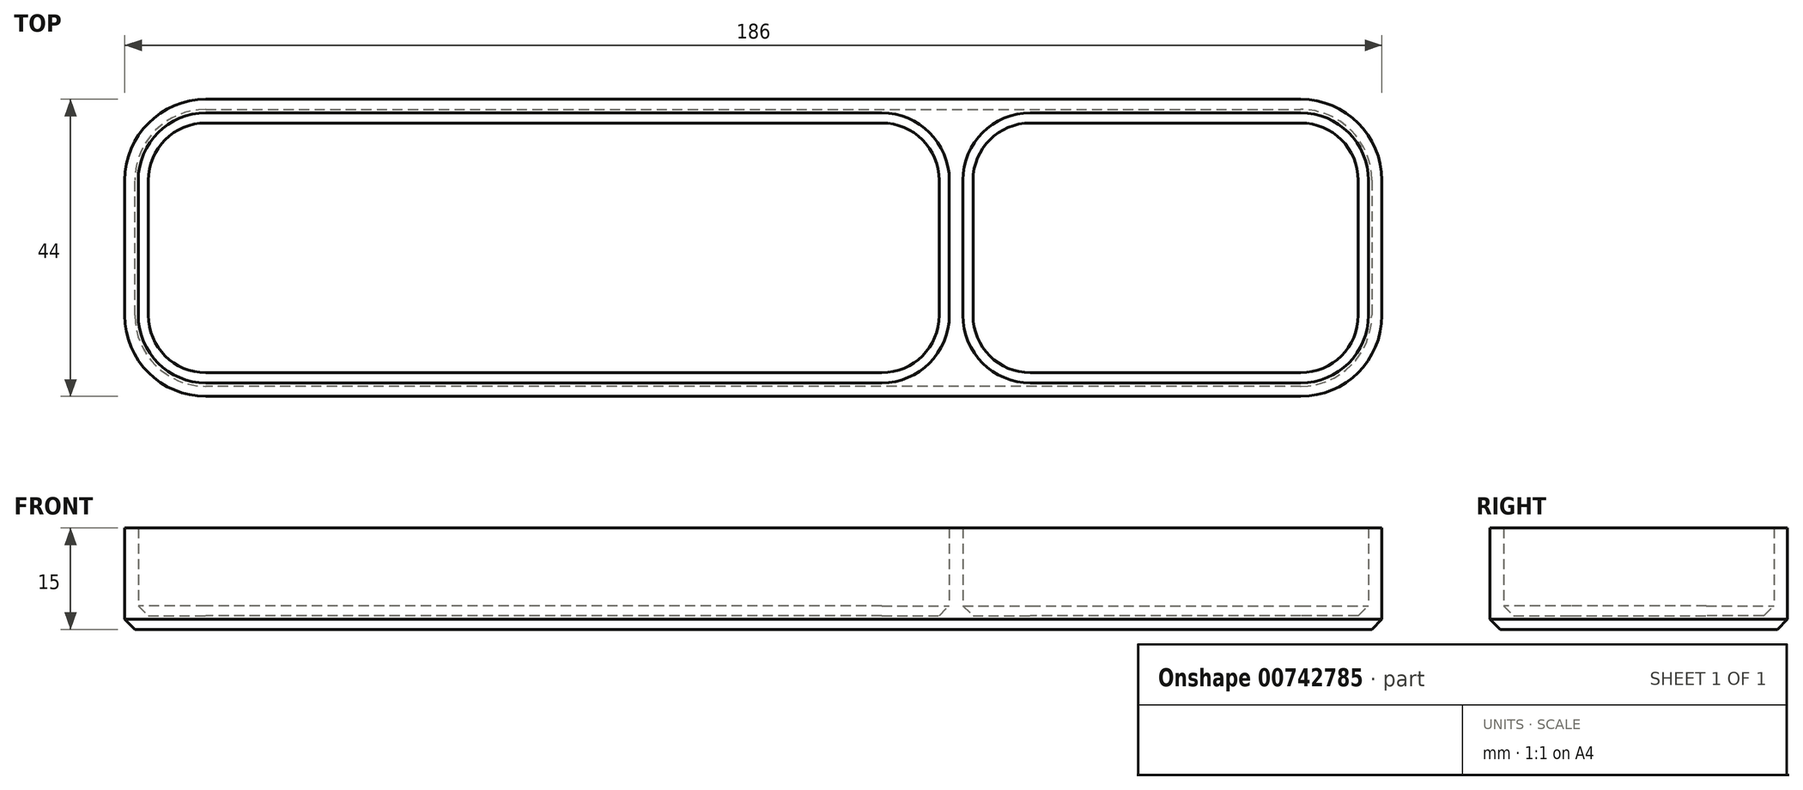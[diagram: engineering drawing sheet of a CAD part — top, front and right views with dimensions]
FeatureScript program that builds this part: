
annotation { "Feature Type Name" : "Feature", "Feature Type Description" : "" }
export const myFeature = defineFeature(function(context is Context, id is Id, definition is map)
    precondition{}
    {
        {
            var Q0;
            Q0=qCreatedBy(makeId("Top.planeOp"),FACE);
            var sketch = newSketch(context, id + "F0", { "sketchPlane" : qUnion([Q0])});
            skLineSegment(sketch, "E0.bottom", {"start": v(10, 0) * mm, "end": v(110, 0) * mm});
            skLineSegment(sketch, "E0.top", {"start": v(10, 40) * mm, "end": v(110, 40) * mm});
            skLineSegment(sketch, "E0.left", {"start": v(0, 10) * mm, "end": v(0, 30) * mm});
            skLineSegment(sketch, "E0.right", {"start": v(120, 10) * mm, "end": v(120, 30) * mm});
            skLineSegment(sketch, "E1.bottom", {"start": v(132, 40) * mm, "end": v(172, 40) * mm});
            skLineSegment(sketch, "E1.top", {"start": v(132, 0) * mm, "end": v(172, 0) * mm});
            skLineSegment(sketch, "E1.left", {"start": v(122, 30) * mm, "end": v(122, 10) * mm});
            skLineSegment(sketch, "E1.right", {"start": v(182, 30) * mm, "end": v(182, 10) * mm});
            skPoint(sketch, "E2.visualSharp", {"position": v(0, 40) * mm});
            skArc(sketch, "E2.filletArc", {"start": v(10, 40) * mm, "mid": v(2.93, 37.07) * mm, "end": v(0, 30) * mm});
            skPoint(sketch, "E3.visualSharp", {"position": v(120, 40) * mm});
            skArc(sketch, "E3.filletArc", {"start": v(120, 30) * mm, "mid": v(117.07, 37.07) * mm, "end": v(110, 40) * mm});
            skPoint(sketch, "E4.visualSharp", {"position": v(120, 0) * mm});
            skArc(sketch, "E4.filletArc", {"start": v(110, 0) * mm, "mid": v(117.07, 2.93) * mm, "end": v(120, 10) * mm});
            skPoint(sketch, "E5.visualSharp", {"position": v(0, 0) * mm});
            skArc(sketch, "E5.filletArc", {"start": v(0, 10) * mm, "mid": v(2.93, 2.93) * mm, "end": v(10, 0) * mm});
            skPoint(sketch, "E6.visualSharp", {"position": v(122, 40) * mm});
            skArc(sketch, "E6.filletArc", {"start": v(132, 40) * mm, "mid": v(124.93, 37.07) * mm, "end": v(122, 30) * mm});
            skPoint(sketch, "E7.visualSharp", {"position": v(122, 0) * mm});
            skArc(sketch, "E7.filletArc", {"start": v(122, 10) * mm, "mid": v(124.93, 2.93) * mm, "end": v(132, 0) * mm});
            skPoint(sketch, "E8.visualSharp", {"position": v(182, 40) * mm});
            skArc(sketch, "E8.filletArc", {"start": v(182, 30) * mm, "mid": v(179.07, 37.07) * mm, "end": v(172, 40) * mm});
            skPoint(sketch, "E9.visualSharp", {"position": v(182, 0) * mm});
            skArc(sketch, "E9.filletArc", {"start": v(172, 0) * mm, "mid": v(179.07, 2.93) * mm, "end": v(182, 10) * mm});
            skLineSegment(sketch, "E10.bottom", {"start": v(-2, 42) * mm, "end": v(184, 42) * mm});
            skLineSegment(sketch, "E10.top", {"start": v(-2, -2) * mm, "end": v(184, -2) * mm});
            skLineSegment(sketch, "E10.left", {"start": v(-2, 42) * mm, "end": v(-2, -2) * mm});
            skLineSegment(sketch, "E10.right", {"start": v(184, 42) * mm, "end": v(184, -2) * mm});
            skSolve(sketch);
        }
        {
            var Q0;
            Q0 = qSketchRegion(id + "F0", true);
            extrude(context, id + "F1", {"entities" : qUnion([Q0]), "depth" : 15 * mm, "offsetDistance" : 25 * mm});
        }
        {
            var Q0;
            Q0=makeQuery(id+"F1.opExtrude","CAP_FACE",FACE,{"disambiguationData":[OSD([sQuery(id+"F0.wireOp",EDGE,"E0.bottom"),sQuery(id+"F0.wireOp",EDGE,"E0.top"),sQuery(id+"F0.wireOp",EDGE,"E0.left"),sQuery(id+"F0.wireOp",EDGE,"E0.right"),sQuery(id+"F0.wireOp",EDGE,"E1.bottom"),sQuery(id+"F0.wireOp",EDGE,"E1.top"),sQuery(id+"F0.wireOp",EDGE,"E1.left"),sQuery(id+"F0.wireOp",EDGE,"E1.right"),sQuery(id+"F0.wireOp",EDGE,"E2.filletArc"),sQuery(id+"F0.wireOp",EDGE,"E3.filletArc"),sQuery(id+"F0.wireOp",EDGE,"E4.filletArc"),sQuery(id+"F0.wireOp",EDGE,"E5.filletArc"),sQuery(id+"F0.wireOp",EDGE,"E6.filletArc"),sQuery(id+"F0.wireOp",EDGE,"E7.filletArc"),sQuery(id+"F0.wireOp",EDGE,"E8.filletArc"),sQuery(id+"F0.wireOp",EDGE,"E9.filletArc"),sQuery(id+"F0.wireOp",EDGE,"E10.bottom"),sQuery(id+"F0.wireOp",EDGE,"E10.top"),sQuery(id+"F0.wireOp",EDGE,"E10.left"),sQuery(id+"F0.wireOp",EDGE,"E10.right")])],"isStart":true});
            var sketch = newSketch(context, id + "F2", { "sketchPlane" : qUnion([Q0])});
            skLineSegment(sketch, "E11.bottom", {"start": v(-2, 2) * mm, "end": v(184, 2) * mm});
            skLineSegment(sketch, "E11.top", {"start": v(-2, -42) * mm, "end": v(184, -42) * mm});
            skLineSegment(sketch, "E11.left", {"start": v(-2, 2) * mm, "end": v(-2, -42) * mm});
            skLineSegment(sketch, "E11.right", {"start": v(184, 2) * mm, "end": v(184, -42) * mm});
            skSolve(sketch);
        }
        {
            var Q0;
            Q0 = qSketchRegion(id + "F2", true);
            extrude(context, id + "F3", {"entities" : qUnion([Q0]), "operationType" : NewBodyOperationType.ADD, "oppositeDirection" : true, "depth" : 2 * mm, "offsetDistance" : 25 * mm});
        }
        {
            var Q0;
            Q0=makeQuery(id+"F1.opExtrude","SWEPT_EDGE",EDGE,{"disambiguationData":[OSD([sQuery(id+"F0.wireOp",EDGE,"E10.top"),sQuery(id+"F0.wireOp",EDGE,"E10.left")])]});
            var Q1;
            Q1=makeQuery(id+"F1.opExtrude","SWEPT_EDGE",EDGE,{"disambiguationData":[OSD([sQuery(id+"F0.wireOp",EDGE,"E10.bottom"),sQuery(id+"F0.wireOp",EDGE,"E10.left")])]});
            var Q2;
            Q2=makeQuery(id+"F1.opExtrude","SWEPT_EDGE",EDGE,{"disambiguationData":[OSD([sQuery(id+"F0.wireOp",EDGE,"E10.top"),sQuery(id+"F0.wireOp",EDGE,"E10.right")])]});
            var Q3;
            Q3=makeQuery(id+"F1.opExtrude","SWEPT_EDGE",EDGE,{"disambiguationData":[OSD([sQuery(id+"F0.wireOp",EDGE,"E10.bottom"),sQuery(id+"F0.wireOp",EDGE,"E10.right")])]});
            fillet(context, id + "F4", {"entities" : qUnion([Q0, Q1, Q2, Q3]), "radius" : 12 * mm, "tangentPropagation" : true, "allowEdgeOverflow" : false});
        }
        {
            var Q0;
            Q0=makeQuery(id+"F3.boolean.opBoolean","SPLIT",FACE,{"disambiguationData":[TD([makeQuery(id+"F1.opExtrude","SWEPT_FACE",FACE,{"disambiguationData":[OSD([sQuery(id+"F0.wireOp",EDGE,"E0.bottom")])]})])],"derivedFrom":makeQuery(id+"F3.opExtrude","CAP_FACE",FACE,{"disambiguationData":[OSD([sQuery(id+"F2.wireOp",EDGE,"E11.bottom"),sQuery(id+"F2.wireOp",EDGE,"E11.top"),sQuery(id+"F2.wireOp",EDGE,"E11.left"),sQuery(id+"F2.wireOp",EDGE,"E11.right")])],"isStart":false})});
            var Q1;
            {var subQ3=makeQuery(id+"F1.opExtrude","SWEPT_FACE",FACE,{"disambiguationData":[OSD([sQuery(id+"F0.wireOp",EDGE,"E1.bottom")])]});Q1=makeQuery(id+"FU2WIVJNVQVhmx0_1.boolean.opBoolean","SPLIT",FACE,{"disambiguationData":[TD([subQ3])],"derivedFrom":makeQuery(id+"F3.boolean.opBoolean","SPLIT",FACE,{"disambiguationData":[TD([subQ3])],"derivedFrom":makeQuery(id+"F3.opExtrude","CAP_FACE",FACE,{"disambiguationData":[OSD([sQuery(id+"F2.wireOp",EDGE,"E11.bottom"),sQuery(id+"F2.wireOp",EDGE,"E11.top"),sQuery(id+"F2.wireOp",EDGE,"E11.left"),sQuery(id+"F2.wireOp",EDGE,"E11.right")])],"isStart":false})})});}
            var Q2;
            {var subQ0=sQuery(id+"F0.wireOp",EDGE,"E10.right");var subQ1=sQuery(id+"F0.wireOp",EDGE,"E10.top");Q2=makeQuery(id+"F4.opFillet","BLEND_EDGE",EDGE,{"blendedFrom":[makeQuery(id+"F1.opExtrude","SWEPT_EDGE",EDGE,{"disambiguationData":[OSD([subQ1,subQ0])]}),makeQuery(id+"F3.boolean.opBoolean","MERGE",FACE,{"derivedFrom":[makeQuery(id+"F1.opExtrude","CAP_FACE",FACE,{"disambiguationData":[OSD([sQuery(id+"F0.wireOp",EDGE,"E0.bottom"),sQuery(id+"F0.wireOp",EDGE,"E0.top"),sQuery(id+"F0.wireOp",EDGE,"E0.left"),sQuery(id+"F0.wireOp",EDGE,"E0.right"),sQuery(id+"F0.wireOp",EDGE,"E1.bottom"),sQuery(id+"F0.wireOp",EDGE,"E1.top"),sQuery(id+"F0.wireOp",EDGE,"E1.left"),sQuery(id+"F0.wireOp",EDGE,"E1.right"),sQuery(id+"F0.wireOp",EDGE,"E2.filletArc"),sQuery(id+"F0.wireOp",EDGE,"E3.filletArc"),sQuery(id+"F0.wireOp",EDGE,"E4.filletArc"),sQuery(id+"F0.wireOp",EDGE,"E5.filletArc"),sQuery(id+"F0.wireOp",EDGE,"E6.filletArc"),sQuery(id+"F0.wireOp",EDGE,"E7.filletArc"),sQuery(id+"F0.wireOp",EDGE,"E8.filletArc"),sQuery(id+"F0.wireOp",EDGE,"E9.filletArc"),sQuery(id+"F0.wireOp",EDGE,"E10.bottom"),subQ1,sQuery(id+"F0.wireOp",EDGE,"E10.left"),subQ0])],"isStart":true}),makeQuery(id+"F3.opExtrude","CAP_FACE",FACE,{"disambiguationData":[OSD([sQuery(id+"F2.wireOp",EDGE,"E11.bottom"),sQuery(id+"F2.wireOp",EDGE,"E11.top"),sQuery(id+"F2.wireOp",EDGE,"E11.left"),sQuery(id+"F2.wireOp",EDGE,"E11.right")])],"isStart":true})]})],"blendedInto":[makeQuery(id+"F3.boolean.opBoolean","MERGE",FACE,{"derivedFrom":[makeQuery(id+"F1.opExtrude","CAP_FACE",FACE,{"disambiguationData":[OSD([sQuery(id+"F0.wireOp",EDGE,"E0.bottom"),sQuery(id+"F0.wireOp",EDGE,"E0.top"),sQuery(id+"F0.wireOp",EDGE,"E0.left"),sQuery(id+"F0.wireOp",EDGE,"E0.right"),sQuery(id+"F0.wireOp",EDGE,"E1.bottom"),sQuery(id+"F0.wireOp",EDGE,"E1.top"),sQuery(id+"F0.wireOp",EDGE,"E1.left"),sQuery(id+"F0.wireOp",EDGE,"E1.right"),sQuery(id+"F0.wireOp",EDGE,"E2.filletArc"),sQuery(id+"F0.wireOp",EDGE,"E3.filletArc"),sQuery(id+"F0.wireOp",EDGE,"E4.filletArc"),sQuery(id+"F0.wireOp",EDGE,"E5.filletArc"),sQuery(id+"F0.wireOp",EDGE,"E6.filletArc"),sQuery(id+"F0.wireOp",EDGE,"E7.filletArc"),sQuery(id+"F0.wireOp",EDGE,"E8.filletArc"),sQuery(id+"F0.wireOp",EDGE,"E9.filletArc"),sQuery(id+"F0.wireOp",EDGE,"E10.bottom"),subQ1,sQuery(id+"F0.wireOp",EDGE,"E10.left"),subQ0])],"isStart":true}),makeQuery(id+"F3.opExtrude","CAP_FACE",FACE,{"disambiguationData":[OSD([sQuery(id+"F2.wireOp",EDGE,"E11.bottom"),sQuery(id+"F2.wireOp",EDGE,"E11.top"),sQuery(id+"F2.wireOp",EDGE,"E11.left"),sQuery(id+"F2.wireOp",EDGE,"E11.right")])],"isStart":true})]})]});}
            chamfer(context, id + "F5", {"entities" : qUnion([Q0, Q1, Q2]), "width" : 1.5 * mm, "tangentPropagation" : true});
        }
    });
